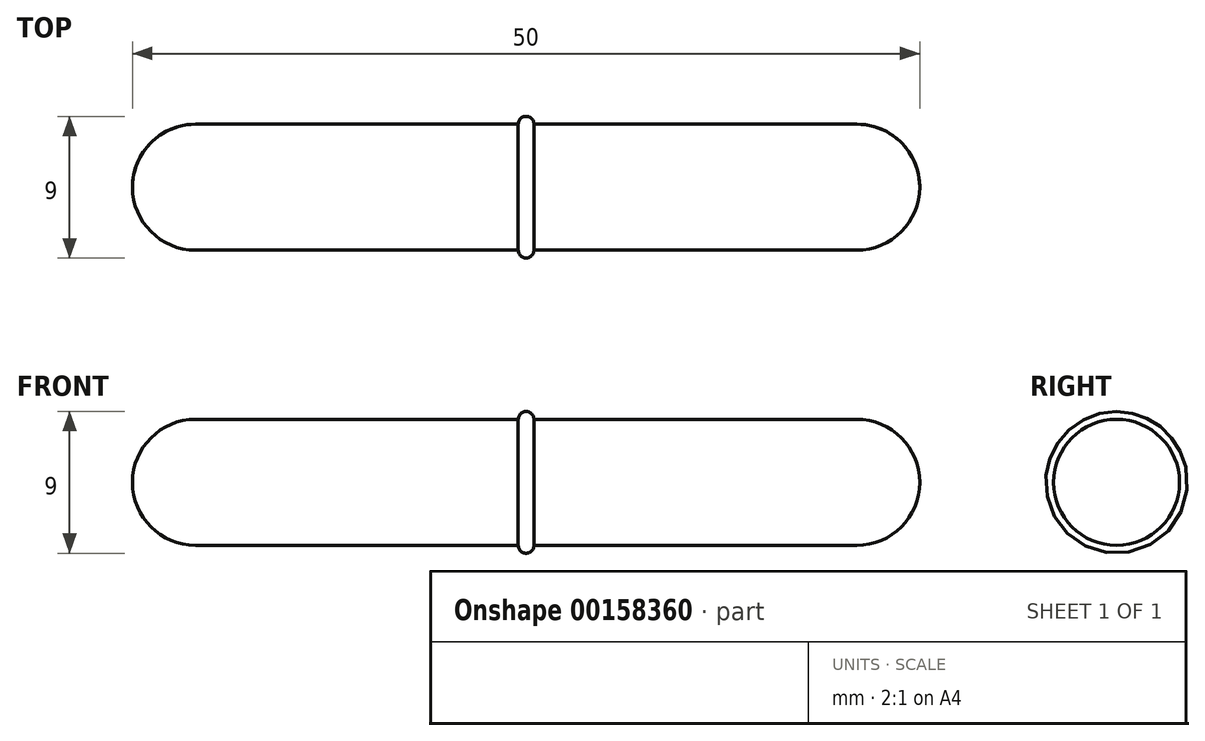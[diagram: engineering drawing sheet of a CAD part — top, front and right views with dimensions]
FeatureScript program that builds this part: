
annotation { "Feature Type Name" : "Feature", "Feature Type Description" : "" }
export const myFeature = defineFeature(function(context is Context, id is Id, definition is map)
    precondition{}
    {
        {
            var Q0;
            Q0=qCreatedBy(makeId("Top.planeOp"),FACE);
            var sketch = newSketch(context, id + "F0", { "sketchPlane" : qUnion([Q0])});
            skLineSegment(sketch, "E0", {"start": v(0, 0) * mm, "end": v(21, 0) * mm});
            skArc(sketch, "E1", {"start": v(25, 0) * mm, "mid": v(23.83, 2.83) * mm, "end": v(21, 4) * mm});
            skLineSegment(sketch, "E2", {"start": v(21, 4) * mm, "end": v(0, 4) * mm});
            skArc(sketch, "E3", {"start": v(0.5, 4) * mm, "mid": v(0.35, 4.35) * mm, "end": v(0, 4.5) * mm});
            skLineSegment(sketch, "E4", {"start": v(25, 0) * mm, "end": v(21, 0) * mm});
            skLineSegment(sketch, "E5", {"start": v(0, 4.5) * mm, "end": v(0, 0) * mm});
            skSolve(sketch);
        }
        {
            var Q0;
            Q0 = qSketchRegion(id + "F0", true);
            var Q1;
            Q1=sQuery(id+"F0.wireOp",EDGE,"E0");
            revolve(context, id + "F1", {"entities" : qUnion([Q0]), "axis" : qUnion([Q1]), "revolveType" : RevolveType.FULL});
        }
        {
            var Q0;
            Q0=makeQuery(id+"F1.opRevolve","SWEPT_BODY",BODY,{"disambiguationData":[OSD([sQuery(id+"F0.wireOp",EDGE,"E0"),sQuery(id+"F0.wireOp",EDGE,"E1"),sQuery(id+"F0.wireOp",EDGE,"E2"),sQuery(id+"F0.wireOp",EDGE,"E3"),sQuery(id+"F0.wireOp",EDGE,"E4"),sQuery(id+"F0.wireOp",EDGE,"E5")])]});
            var Q1;
            Q1=makeQuery(id+"F1.opRevolve","SWEPT_FACE",FACE,{"disambiguationData":[OSD([sQuery(id+"F0.wireOp",EDGE,"E5")])]});
            mirror(context, id + "F2", {"operationType" : NewBodyOperationType.ADD, "entities" : qUnion([Q0]), "mirrorPlane" : qUnion([Q1])});
        }
        {
            var Q0;
            Q0=qCreatedBy(makeId("Front.planeOp"),FACE);
            var sketch = newSketch(context, id + "F3", { "sketchPlane" : qUnion([Q0])});
            skLineSegment(sketch, "E6", {"start": v(0, 0) * mm, "end": v(0, 4.74) * mm, "construction": true});
            skSolve(sketch);
        }
    });
